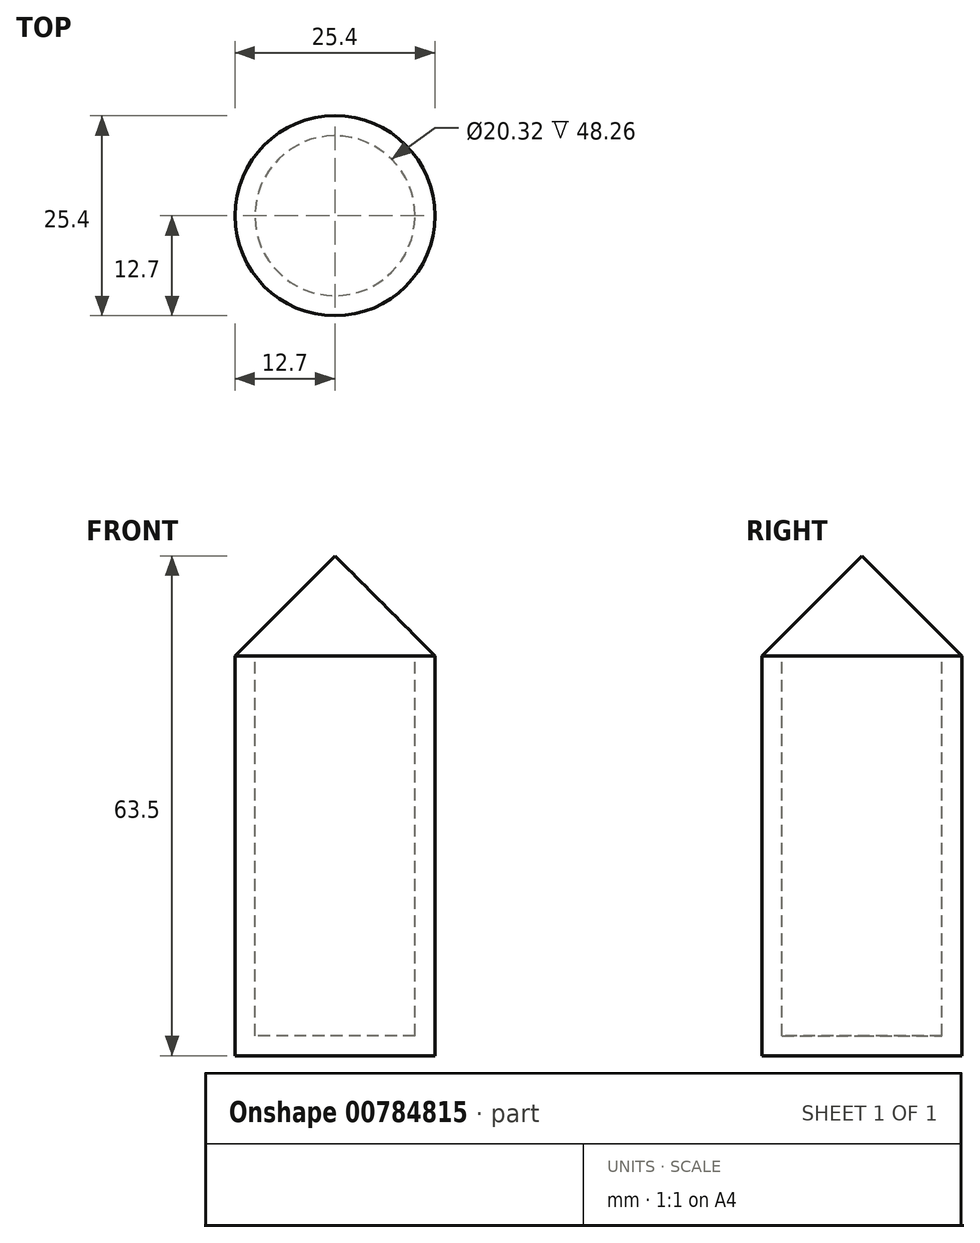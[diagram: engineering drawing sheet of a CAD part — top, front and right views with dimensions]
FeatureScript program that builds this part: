
annotation { "Feature Type Name" : "Feature", "Feature Type Description" : "" }
export const myFeature = defineFeature(function(context is Context, id is Id, definition is map)
    precondition{}
    {
        {
            var Q0;
            Q0=qCreatedBy(makeId("Top.planeOp"),FACE);
            var sketch = newSketch(context, id + "F0", { "sketchPlane" : qUnion([Q0])});
            skCircle(sketch, "E0", {"center": v(0, 0) * mm, "radius": 12.7 * mm});
            skSolve(sketch);
        }
        {
            var Q0;
            Q0 = qSketchRegion(id + "F0", true);
            extrude(context, id + "F1", {"entities" : qUnion([Q0]), "depth" : 50.8 * mm, "offsetDistance" : 25.4 * mm});
        }
        {
            var Q0;
            Q0=makeQuery(id+"F1.opExtrude","CAP_FACE",FACE,{"disambiguationData":[OSD([sQuery(id+"F0.wireOp",EDGE,"E0")])],"isStart":false});
            var sketch = newSketch(context, id + "F2", { "sketchPlane" : qUnion([Q0])});
            skCircle(sketch, "E1", {"center": v(0, 0) * mm, "radius": 10.16 * mm});
            skSolve(sketch);
        }
        {
            var Q0;
            Q0 = qSketchRegion(id + "F2", true);
            extrude(context, id + "F3", {"entities" : qUnion([Q0]), "operationType" : NewBodyOperationType.REMOVE, "oppositeDirection" : true, "depth" : 48.26 * mm, "offsetDistance" : 25.4 * mm});
        }
        {
            var Q0;
            Q0=makeQuery(id+"F1.opExtrude","CAP_FACE",FACE,{"disambiguationData":[OSD([sQuery(id+"F0.wireOp",EDGE,"E0")])],"isStart":false});
            var sketch = newSketch(context, id + "F4", { "sketchPlane" : qUnion([Q0])});
            skCircle(sketch, "E2", {"center": v(0, 0) * mm, "radius": 12.7 * mm});
            skSolve(sketch);
        }
        {
            var Q0;
            Q0 = qSketchRegion(id + "F4", true);
            extrude(context, id + "F5", {"entities" : qUnion([Q0]), "operationType" : NewBodyOperationType.ADD, "depth" : 25.4 * mm, "offsetDistance" : 25.4 * mm, "hasDraft" : true, "draftAngle" : 45 * degree, "draftPullDirection" : true});
        }
    });
